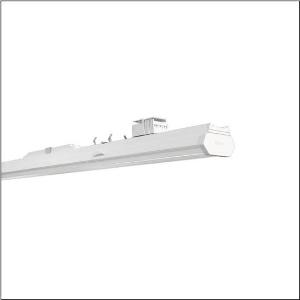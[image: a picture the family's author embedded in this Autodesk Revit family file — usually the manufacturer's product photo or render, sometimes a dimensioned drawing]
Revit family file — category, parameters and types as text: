
# Revit family: licross_r__21_protected_ho_52td1bcn4b5m_1c3e
name_source: partatom
category: Lighting Fixtures
units: mm (PartAtom-declared; Revit-internal decimal feet)

## family parameters
Cut with Voids When Loaded = No
Host = Face
Light Source = No
Part Type = Normal
Room Calculation Point = No
Round Connector Dimension = Use Diameter
Shared = No

## types (1)
- --- (1 x LED, 11820 lm, 68.9 W, 4000K)
    Apparent Load = 69 VA
    CIE Flux Codes = 54 82 95 97 100
    Color Rendering = 80
    Color Temperature = 4000K
    Default Elevation = 1800 mm
    Description = Licross® 21 Protected HO, luminaire insert, of sheet steel, galvanised, coil coated, white, length: 1.500mm, width: 90mm, height: 103mm, LED rated luminous flux: 11.830lm, light colour: 840, control gear: ON/OFF Multilumen, CLOi, control gear: ECG Multilumen, with plug, 3-pole, with phase selection, mains connection: 220..240V, AC, 50/60Hz, start of lifetime: 69W, end of service life: 83W, halogen-free wiring, primary optical cover: cover, of PMMA, light emission: direct distribution, primary light characteristic: symmetric, protection rating (complete): IP54, insulation class (complete): insulation class I (protective earthing), certification: CE, ENEC, VDE, UKCA, protection symbol: D if used in an environment with non-conductive dust loads with corresponding accessories, impact resistance: IK06, permissible ambient temperature for indoor applications: -35..+35°C, corresponds to IFS (International Featured Standards) requirements for safety and quality in the food industry, reducing of maximum allowable ambient temperature of 5°C with ceiling mounting, LABS conformity tested according to VDMA 24364:2018-05, packaging unit: 1 piece
    Height = 92 mm
    Lamp = 1 x LED
    Lamp Light Flux = 11820 lm
    Lamp Power = 68.9 W
    Lamp count = 1
    Length = 1500 mm
    Luminous efficacy = 172 lm/W
    Manufacturer = Siteco
    ModVariant = No
    Model = 52TD1BCN4B5M
    Mounting Place = Ceiling
    Mounting Type = Pendant
    Number of Poles = 1
    OnlyDefault = Yes
    Power Factor = 1
    Product Name = Licross® 21 Protected HO
    Product group = luminaire insert
    ProductGroupID = 901
    Protection Class = Protection class I
    Protection Degree = IP 54
    RLX_Detail_Level = 1
    RLX_Emergency_Light_Flux = 0 lm
    RLX_Emergency_Type = 0
    RLX_Emergency_Type_DB = No
    RlxData = <blob elided: 22077 chars, md5=5b498d6e>
    Socket = socket
    Standby Power = 0 W
    System Light Flux = 11820 lm
    System Power = 69 W
    Type Comments = factory setting: luminous flux: 100 % | (A | C | E) | 162 mA
    Type Image = l_1256148.jpg
    URL = http://relux.com
    VarID = @adj_041617
    Voltage = 0 V
    Weight = 0.00 kg
    Width = 88 mm

## geometry (parser evidence)
native form markers: Blend x4, Sweep x9
no freeform markers — native parametric forms only
